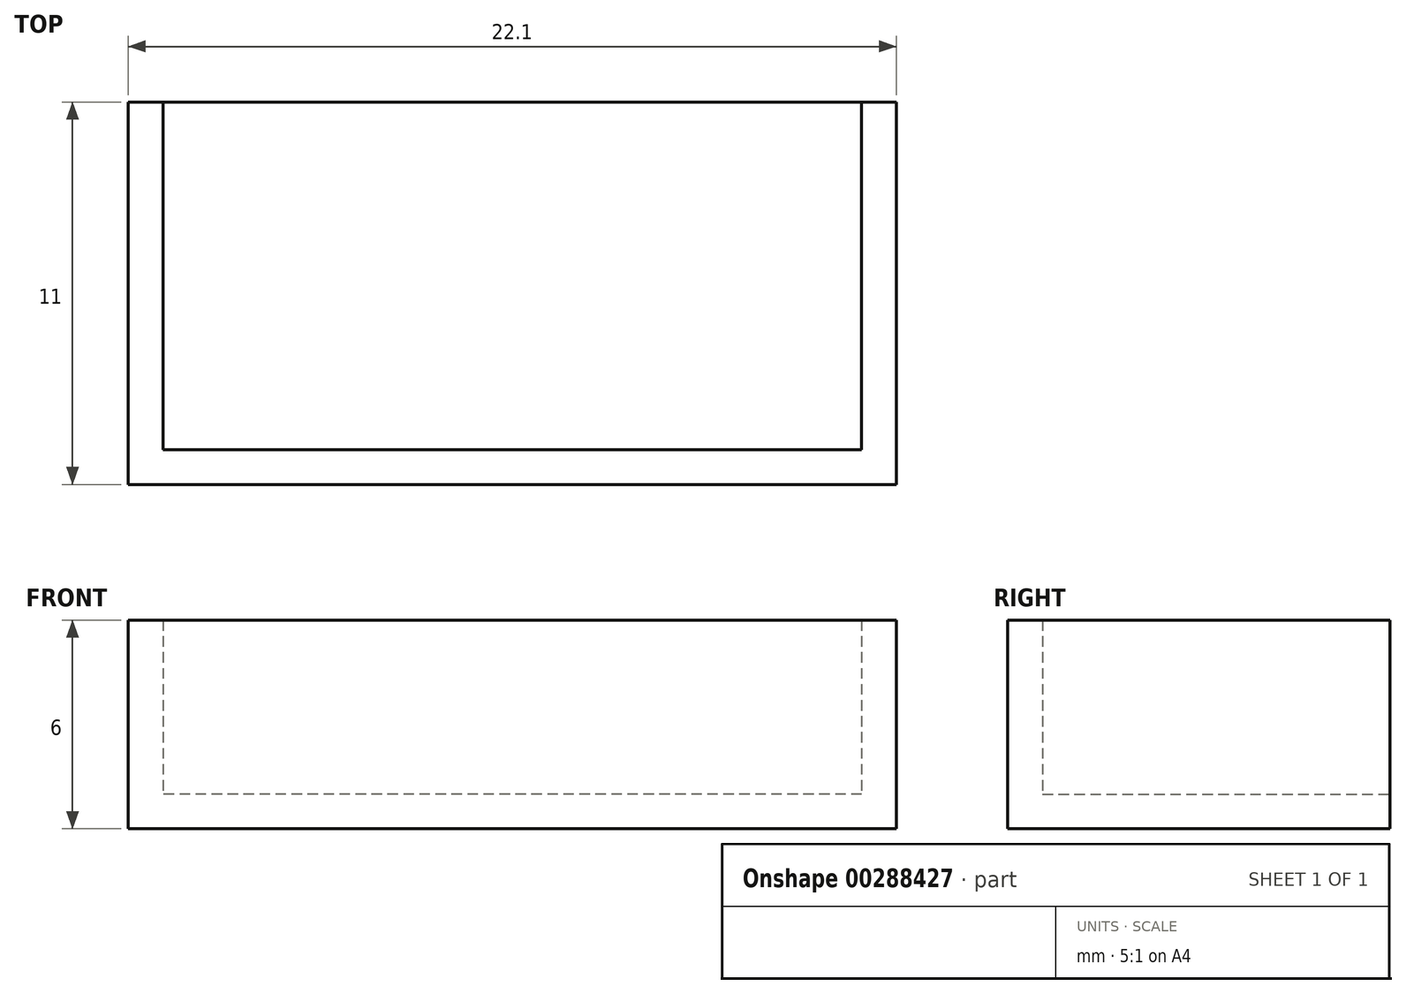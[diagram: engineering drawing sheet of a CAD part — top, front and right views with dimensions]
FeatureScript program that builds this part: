
annotation { "Feature Type Name" : "Feature", "Feature Type Description" : "" }
export const myFeature = defineFeature(function(context is Context, id is Id, definition is map)
    precondition{}
    {
        {
            var Q0;
            Q0=qCreatedBy(makeId("Top.planeOp"),FACE);
            var sketch = newSketch(context, id + "F0", { "sketchPlane" : qUnion([Q0])});
            skLineSegment(sketch, "E0.bottom", {"start": v(10.05, -5) * mm, "end": v(-10.05, -5) * mm});
            skLineSegment(sketch, "E0.top", {"start": v(10.05, 5) * mm, "end": v(-10.05, 5) * mm});
            skLineSegment(sketch, "E0.left", {"start": v(10.05, -5) * mm, "end": v(10.05, 5) * mm});
            skLineSegment(sketch, "E0.right", {"start": v(-10.05, -5) * mm, "end": v(-10.05, 5) * mm});
            skPoint(sketch, "E0.middle", {"position": v(0, 0) * mm});
            skLineSegment(sketch, "E1.0", {"start": v(-11.05, -6) * mm, "end": v(-11.05, 5) * mm});
            skLineSegment(sketch, "E1.1", {"start": v(11.05, -6) * mm, "end": v(-11.05, -6) * mm});
            skLineSegment(sketch, "E1.2", {"start": v(11.05, -6) * mm, "end": v(11.05, 5) * mm});
            skLineSegment(sketch, "E2", {"start": v(-11.05, 5) * mm, "end": v(-10.05, 5) * mm});
            skLineSegment(sketch, "E3", {"start": v(10.05, 5) * mm, "end": v(11.05, 5) * mm});
            skSolve(sketch);
        }
        {
            var Q0;
            Q0=makeQuery(id+"F0.imprint","IMPRINT",FACE,{"disambiguationData":[TD([[makeQuery(id+"F0.imprint","IMPRINT",EDGE,{"derivedFrom":sQuery(id+"F0.wireOp",EDGE,"E0.bottom")}),-1.0]])]});
            extrude(context, id + "F1", {"entities" : qUnion([Q0]), "depth" : 1 * mm});
        }
        {
            var Q0;
            Q0=makeQuery(id+"F0.imprint","IMPRINT",FACE,{"disambiguationData":[TD([[makeQuery(id+"F0.imprint","IMPRINT",EDGE,{"derivedFrom":sQuery(id+"F0.wireOp",EDGE,"E0.bottom")}),1.0]])]});
            extrude(context, id + "F2", {"entities" : qUnion([Q0]), "operationType" : NewBodyOperationType.ADD, "depth" : 6 * mm});
        }
    });
